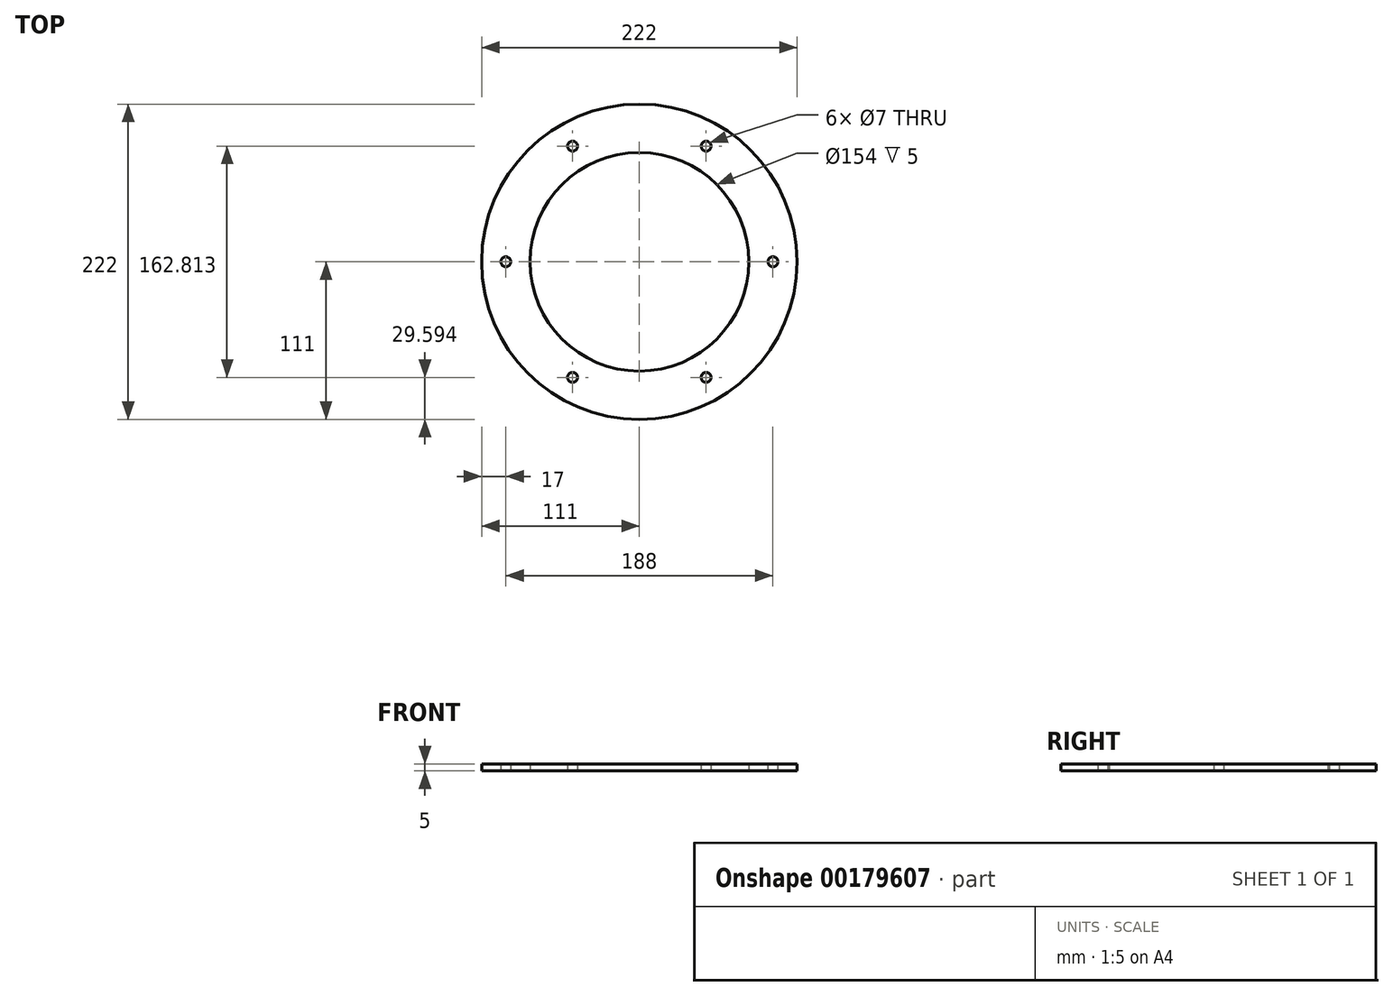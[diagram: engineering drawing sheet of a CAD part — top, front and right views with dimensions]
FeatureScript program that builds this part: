
annotation { "Feature Type Name" : "Feature", "Feature Type Description" : "" }
export const myFeature = defineFeature(function(context is Context, id is Id, definition is map)
    precondition{}
    {
        {
            var Q0;
            Q0=qCreatedBy(makeId("Top.planeOp"),FACE);
            var sketch = newSketch(context, id + "F0", { "sketchPlane" : qUnion([Q0])});
            skCircle(sketch, "E0", {"center": v(0, 0) * mm, "radius": 111 * mm});
            skCircle(sketch, "E1", {"center": v(0, 0) * mm, "radius": 77 * mm});
            skCircle(sketch, "E2", {"center": v(0, 0) * mm, "radius": 94 * mm, "construction": true});
            skPoint(sketch, "E3", {"position": v(-50.45, 87.38) * mm});
            skLineSegment(sketch, "E4", {"start": v(0, 0) * mm, "end": v(-50.45, 87.38) * mm, "construction": true});
            skLineSegment(sketch, "E5.0", {"start": v(-47, 81.4) * mm, "end": v(47, 81.4) * mm, "construction": true});
            skLineSegment(sketch, "E5.1", {"start": v(47, 81.4) * mm, "end": v(94, 0) * mm, "construction": true});
            skLineSegment(sketch, "E5.2", {"start": v(94, 0) * mm, "end": v(47, -81.4) * mm, "construction": true});
            skLineSegment(sketch, "E5.3", {"start": v(47, -81.4) * mm, "end": v(-47, -81.4) * mm, "construction": true});
            skLineSegment(sketch, "E5.4", {"start": v(-47, -81.4) * mm, "end": v(-94, 0) * mm, "construction": true});
            skLineSegment(sketch, "E5.5", {"start": v(-94, 0) * mm, "end": v(-47, 81.4) * mm, "construction": true});
            skCircle(sketch, "E6", {"center": v(-47, 81.4) * mm, "radius": 3.5 * mm});
            skCircle(sketch, "E7", {"center": v(47, 81.4) * mm, "radius": 3.5 * mm});
            skCircle(sketch, "E8", {"center": v(94, 0) * mm, "radius": 3.5 * mm});
            skCircle(sketch, "E9", {"center": v(47, -81.4) * mm, "radius": 3.5 * mm});
            skCircle(sketch, "E10", {"center": v(-47, -81.4) * mm, "radius": 3.5 * mm});
            skCircle(sketch, "E11", {"center": v(-94, 0) * mm, "radius": 3.5 * mm});
            skLineSegment(sketch, "E12", {"start": v(47, 81.4) * mm, "end": v(38.5, 66.68) * mm, "construction": true});
            skLineSegment(sketch, "E13", {"start": v(38.5, 66.68) * mm, "end": v(55.5, 96.13) * mm, "construction": true});
            skSolve(sketch);
        }
        {
            var Q0;
            Q0=makeQuery(id+"F0.imprint","IMPRINT",FACE,{"disambiguationData":[TD([[makeQuery(id+"F0.imprint","IMPRINT",EDGE,{"derivedFrom":sQuery(id+"F0.wireOp",EDGE,"E0")}),1.0]])]});
            extrude(context, id + "F1", {"entities" : qUnion([Q0]), "depth" : 5 * mm});
        }
    });
